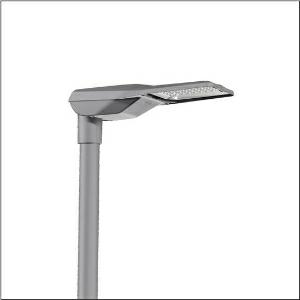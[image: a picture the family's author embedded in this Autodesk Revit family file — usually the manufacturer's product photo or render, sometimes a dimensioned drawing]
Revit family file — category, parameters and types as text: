
# Revit family: streetlight_sl_21_iq_mini___st0_5a_5xe2b41g08gb_465e
name_source: partatom
category: Lighting Fixtures
units: mm (PartAtom-declared; Revit-internal decimal feet)

## family parameters
Cut with Voids When Loaded = No
Host = Face
Light Source = No
Part Type = Normal
Room Calculation Point = No
Round Connector Dimension = Use Diameter
Shared = No

## types (1)
- --- (1 x LED, 5920 lm, 37.1 W, 4000K)
    Apparent Load = 37 VA
    CIE Flux Codes = 41 75 97 100 100
    Color Rendering = 70
    Color Temperature = 4000K
    Default Elevation = 1800 mm
    Description = Streetlight SL 21 iQ mini, mast luminaire, primary light control with lens, of PMMA, primary optical cover: cover, of toughened safety glass, transparent, light distribution: ST0.5a, light emission: direct distribution, primary light characteristic: asymmetric, installation type: post-top, side-entry, LED, High Power LED, rated luminous flux: 5.920lm, luminous efficacy: 160lm/W, light colour: 740, colour temperature: 4000K, control gear: iQ Street-Remote, control: Street-Remote, Auto-Match, Temp-Guard, Lumen-Switch, Night-Set, Smart-Wire, Light-Fading, Desk-Remote (wireless, voltage-free reading and setting of iQ features in the workshop via application-optimized NFC function/RFID function), optimised constant luminous flux control (CLO 2.0), pre-setting: linear dimming characteristic, mains connection: 220..240V, AC, 50/60Hz, start of lifetime: 37W, end of service life: 39W, reduction: 18W, luminaire housing, of diecast aluminium, powder-coated, SITECO metallic grey (DB 702S), corrosivity category C5 high according to DIN EN ISO 12944, please order mast flange separately, inclination adjustable: 0°, 5°, 10°, 15°, sealing non-destructively replaceable, multi-level sealing system, length: 628mm, width: 235mm, height: 110mm, mast flange for spigot size: 42mm (side-entry): 5XC10008XM4, 60/48mm (side-entry/post-top): 5XC10108XM2, 76/60mm (side-entry/post-top): 5XC10108XM1, mounting height: 4..8m, protection rating (complete): IP66, insulation class (complete): insulation class II (safety insulation), certification: CE, ENEC, ENEC+, VDE, impact resistance: IK10, permissible operating ambient temperature for outdoor applications: -40..+50°C, standard-compliant lighting for roads and squares, packaging unit: 1 piece

Light Distribution: ST0.5a
    Height = 110 mm
    Lamp = 1 x LED
    Lamp Light Flux = 5920 lm
    Lamp Power = 37.1 W
    Lamp count = 1
    Length = 625 mm
    Luminous efficacy = 160 lm/W
    Manufacturer = Siteco
    ModVariant = No
    Model = 5XE2B41G08GB
    Number of Poles = 1
    OnlyDefault = Yes
    Power Factor = 1
    Product Name = Streetlight SL 21 iQ mini | ST0.5a
    Product group = mast luminaire | pylon top
    ProductGroupID = 6100
    Protection Class = Protection class II
    Protection Degree = IP 66
    RLX_Detail_Level = 1
    RLX_Emergency_Light_Flux = 0 lm
    RLX_Emergency_Type = 0
    RLX_Emergency_Type_DB = No
    RlxData = <blob elided: 37325 chars, md5=803c7ba8>
    Socket = socket
    Standby Power = 0 W
    System Light Flux = 5920 lm
    System Power = 37 W
    Type Comments = factory setting: luminous flux: 100 % | dim-lin: 254 | 385 mA
    Type Image = l_1003519.jpg
    URL = http://relux.com
    VarID = @adj_188763
    Voltage = 0 V
    Weight = 0.00 kg
    Width = 234 mm

## geometry (parser evidence)
native form markers: Blend x4, Sweep x11
no freeform markers — native parametric forms only
